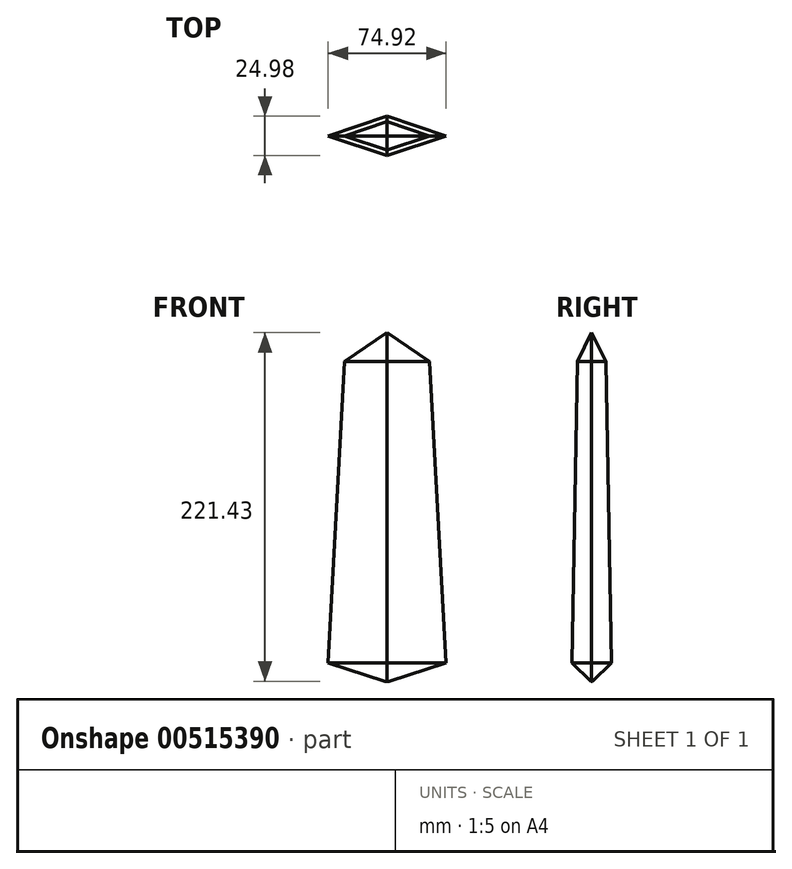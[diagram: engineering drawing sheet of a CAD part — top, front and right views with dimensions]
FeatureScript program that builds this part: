
annotation { "Feature Type Name" : "Feature", "Feature Type Description" : "" }
export const myFeature = defineFeature(function(context is Context, id is Id, definition is map)
    precondition{}
    {
        {
            var Q0;
            Q0=qCreatedBy(makeId("Top.planeOp"),FACE);
            var sketch = newSketch(context, id + "F0", { "sketchPlane" : qUnion([Q0])});
            skLineSegment(sketch, "E0", {"start": v(-38.1, 0) * mm, "end": v(0, 12.7) * mm});
            skLineSegment(sketch, "E1", {"start": v(0, 12.7) * mm, "end": v(38.1, 0) * mm});
            skLineSegment(sketch, "E2", {"start": v(38.1, 0) * mm, "end": v(0, -12.7) * mm});
            skLineSegment(sketch, "E3", {"start": v(0, -12.7) * mm, "end": v(-38.1, 0) * mm});
            skLineSegment(sketch, "E4", {"start": v(0, 0) * mm, "end": v(0, 12.7) * mm, "construction": true});
            skLineSegment(sketch, "E5", {"start": v(0, -12.7) * mm, "end": v(0, 0) * mm, "construction": true});
            skSolve(sketch);
        }
        {
            var Q0;
            Q0 = qSketchRegion(id + "F0", true);
            extrude(context, id + "F1", {"entities" : qUnion([Q0]), "depth" : 203.2 * mm, "offsetDistance" : 25.4 * mm, "hasDraft" : true, "draftAngle" : 1 * degree, "draftPullDirection" : true});
        }
        {
            var Q0;
            Q0=makeQuery(id+"F1.opExtrude","CAP_FACE",FACE,{"disambiguationData":[OSD([sQuery(id+"F0.wireOp",EDGE,"E0"),sQuery(id+"F0.wireOp",EDGE,"E1"),sQuery(id+"F0.wireOp",EDGE,"E2"),sQuery(id+"F0.wireOp",EDGE,"E3")])],"isStart":false});
            extrude(context, id + "F2", {"entities" : qUnion([Q0]), "operationType" : NewBodyOperationType.ADD, "depth" : 25.4 * mm, "offsetDistance" : 25.4 * mm, "hasDraft" : true, "draftAngle" : 25 * degree, "draftPullDirection" : true});
        }
        {
            var Q0;
            Q0=makeQuery(id+"F1.opExtrude","CAP_EDGE",EDGE,{"disambiguationData":[OSD([sQuery(id+"F0.wireOp",EDGE,"E0")])],"isStart":true});
            var Q1;
            Q1=makeQuery(id+"F1.opExtrude","CAP_EDGE",EDGE,{"disambiguationData":[OSD([sQuery(id+"F0.wireOp",EDGE,"E1")])],"isStart":true});
            var Q2;
            Q2=makeQuery(id+"F1.opExtrude","CAP_EDGE",EDGE,{"disambiguationData":[OSD([sQuery(id+"F0.wireOp",EDGE,"E2")])],"isStart":true});
            var Q3;
            Q3=makeQuery(id+"F1.opExtrude","CAP_EDGE",EDGE,{"disambiguationData":[OSD([sQuery(id+"F0.wireOp",EDGE,"E3")])],"isStart":true});
            chamfer(context, id + "F3", {"entities" : qUnion([Q0, Q1, Q2, Q3]), "width" : 11.43 * mm, "tangentPropagation" : true});
        }
    });
